# Revit family: Ulimax_Aluminio_Janela-Max-Ar-Skyfull-45-1-MOD
name_source: partatom
category: Janelas
units: mm (PartAtom-declared; Revit-internal decimal feet)

## family parameters
Compartilhado = Não
Corte com vazios quando carregada = Não
Hospedeiro = Parede
Número OmniClass = 23.30.10.00
Ponto de cálculo do ambiente = Não
Sempre na vertical = Sim
Título OmniClass = Doors

## types (16) — shared parameters
Comentários de tipos = Janela Max Ar Skyfull 45
Construção analítica = <Nenhum>
Definir propriedades térmicas por = Tipo esquemático
Descrição = Janela com esquadria minimalista de alumínio, 1 módulo
Developer = Blocks
Fabricante = Ulimax - Wood & Aluminum
Fechamento da parede = Por hospedeiro
URL = https://www.ulimax.com.br
URL Developer = https://www.BlocksRvt.com
URL Produto = https://www.ulimax.com.br
URL Template = https://www.ulimax.com.br
Visor = Ulimax - Glass - Transparent

## per-type parameters (varying)
| type | Altura | Altura bruta | Caixilho | Largura | Largura bruta | Puxador | a | b |
| Branco - 1.40 x 0.70 | 70 | 79.34 | Ulimax - Metal - White - Matte - 246-246-243 | 140 | 149.34 | Ulimax - Metal - White - Matte - 246-246-243 | 140 | 70 |
| Branco - 1.20 x 0.60 | 60 | 69.34 | Ulimax - Metal - White - Matte - 246-246-243 | 120 | 129.34 | Ulimax - Metal - White - Matte - 246-246-243 | 120 | 60 |
| Branco - 0.70 x 0.70 | 70 | 79.34 | Ulimax - Metal - White - Matte - 246-246-243 | 70 | 79.34 | Ulimax - Metal - White - Matte - 246-246-243 | 70 | 70 |
| Branco - 0.60 x 0.60 | 60 | 69.34 | Ulimax - Metal - White - Matte - 246-246-243 | 60 | 69.34 | Ulimax - Metal - White - Matte - 246-246-243 | 60 | 60 |
| Preto - 1.40 x 0.70 | 70 | 79.34 | Ulimax - Metal - Black - Matte - 15-15-15 | 140 | 149.34 | Ulimax - Metal - Black - Matte - 15-15-15 | 140 | 70 |
| Cinza - 1.40 x 0.70 | 70 | 79.34 | Ulimax - Metal - Chrome - 203-203-203 | 140 | 149.34 | Ulimax - Metal - Chrome - 203-203-203 | 140 | 70 |
| Cinza - 0.60 x 0.60 | 60 | 69.34 | Ulimax - Metal - Chrome - 203-203-203 | 60 | 69.34 | Ulimax - Metal - Chrome - 203-203-203 | 60 | 60 |
| Cinza - 0.70 x 0.70 | 70 | 79.34 | Ulimax - Metal - Chrome - 203-203-203 | 70 | 79.34 | Ulimax - Metal - Chrome - 203-203-203 | 70 | 70 |
| Cinza - 1.20 x 0.60 | 60 | 69.34 | Ulimax - Metal - Chrome - 203-203-203 | 120 | 129.34 | Ulimax - Metal - Chrome - 203-203-203 | 120 | 60 |
| Preto - 1.20 x 0.60 | 60 | 69.34 | Ulimax - Metal - Black - Matte - 15-15-15 | 120 | 129.34 | Ulimax - Metal - Black - Matte - 15-15-15 | 120 | 60 |
| Preto - 0.70 x 0.70 | 70 | 79.34 | Ulimax - Metal - Black - Matte - 15-15-15 | 70 | 79.34 | Ulimax - Metal - Black - Matte - 15-15-15 | 70 | 70 |
| Preto - 0.60 x 0.60 | 60 | 69.34 | Ulimax - Metal - Black - Matte - 15-15-15 | 60 | 69.34 | Ulimax - Metal - Black - Matte - 15-15-15 | 60 | 60 |
| Champanhe - 0.60 x 0.60 | 60 | 69.34 | Ulimax - Metal - Beige - Matte - 230-200-160 | 60 | 69.34 | Ulimax - Metal - Beige - Matte - 230-200-160 | 60 | 60 |
| Champanhe - 0.70 x 0.70 | 70 | 79.34 | Ulimax - Metal - Beige - Matte - 230-200-160 | 70 | 79.34 | Ulimax - Metal - Beige - Matte - 230-200-160 | 70 | 70 |
| Champanhe - 1.20 x 0.60 | 60 | 69.34 | Ulimax - Metal - Beige - Matte - 230-200-160 | 120 | 129.34 | Ulimax - Metal - Beige - Matte - 230-200-160 | 120 | 60 |
| Champanhe - 1.40 x 0.70 | 70 | 79.34 | Ulimax - Metal - Beige - Matte - 230-200-160 | 140 | 149.34 | Ulimax - Metal - Beige - Matte - 230-200-160 | 140 | 70 |
